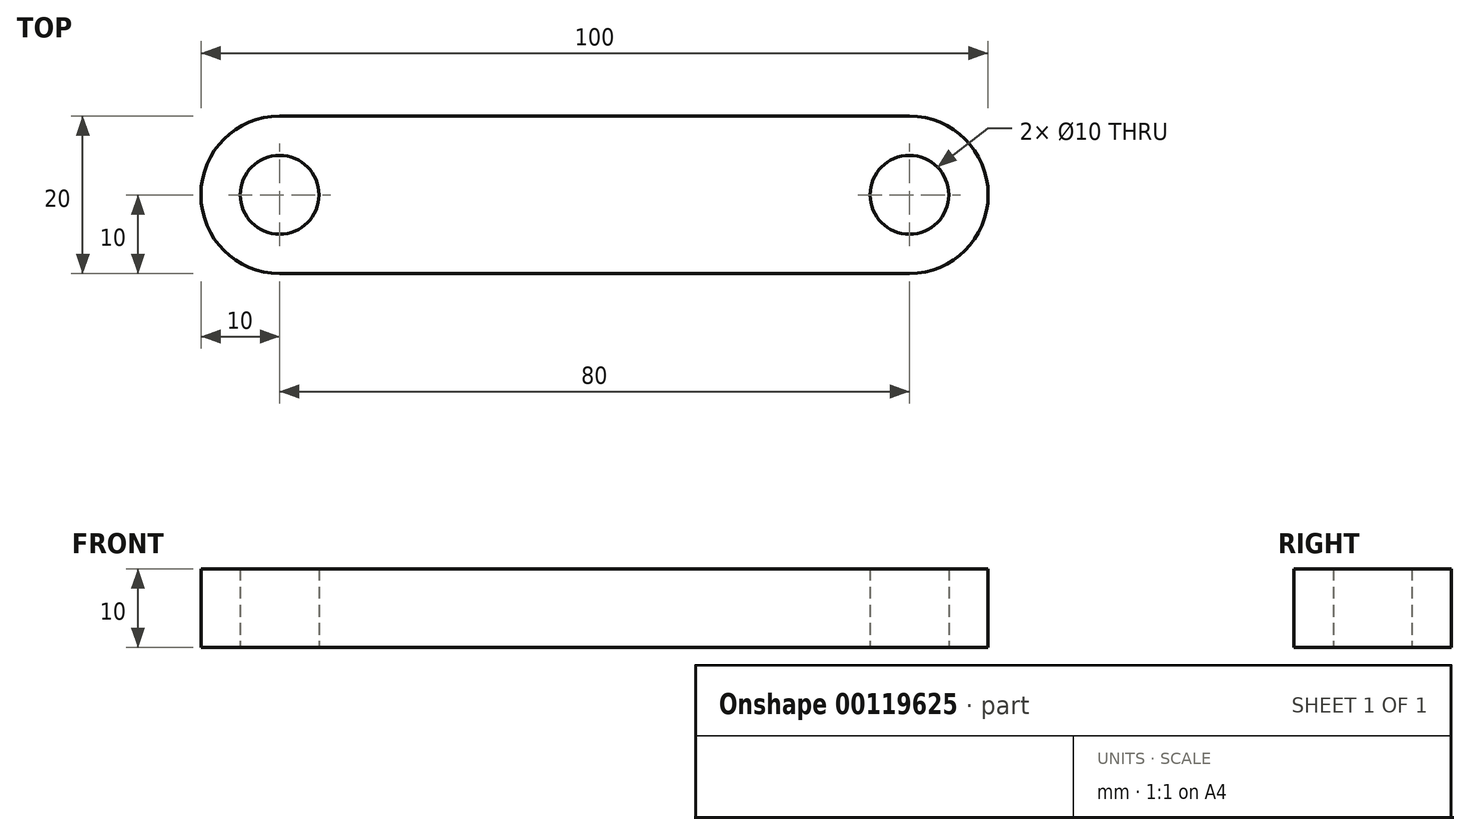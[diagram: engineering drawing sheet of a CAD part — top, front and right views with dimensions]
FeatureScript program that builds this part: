
annotation { "Feature Type Name" : "Feature", "Feature Type Description" : "" }
export const myFeature = defineFeature(function(context is Context, id is Id, definition is map)
    precondition{}
    {
        {
            var Q0;
            Q0=qCreatedBy(makeId("Top.planeOp"),FACE);
            var sketch = newSketch(context, id + "F0", { "sketchPlane" : qUnion([Q0])});
            skLineSegment(sketch, "E0", {"start": v(0, 0) * mm, "end": v(80, 0) * mm});
            skLineSegment(sketch, "E1", {"start": v(0, 20) * mm, "end": v(80, 20) * mm});
            skArc(sketch, "E2", {"start": v(0, 20) * mm, "mid": v(-10, 10) * mm, "end": v(0, 0) * mm});
            skArc(sketch, "E3", {"start": v(80, 0) * mm, "mid": v(90, 10) * mm, "end": v(80, 20) * mm});
            skCircle(sketch, "E4", {"center": v(0, 10) * mm, "radius": 5 * mm});
            skCircle(sketch, "E5", {"center": v(80, 10) * mm, "radius": 5 * mm});
            skSolve(sketch);
        }
        {
            var Q0;
            Q0 = qSketchRegion(id + "F0", true);
            extrude(context, id + "F1", {"entities" : qUnion([Q0]), "depth" : 10 * mm});
        }
    });
